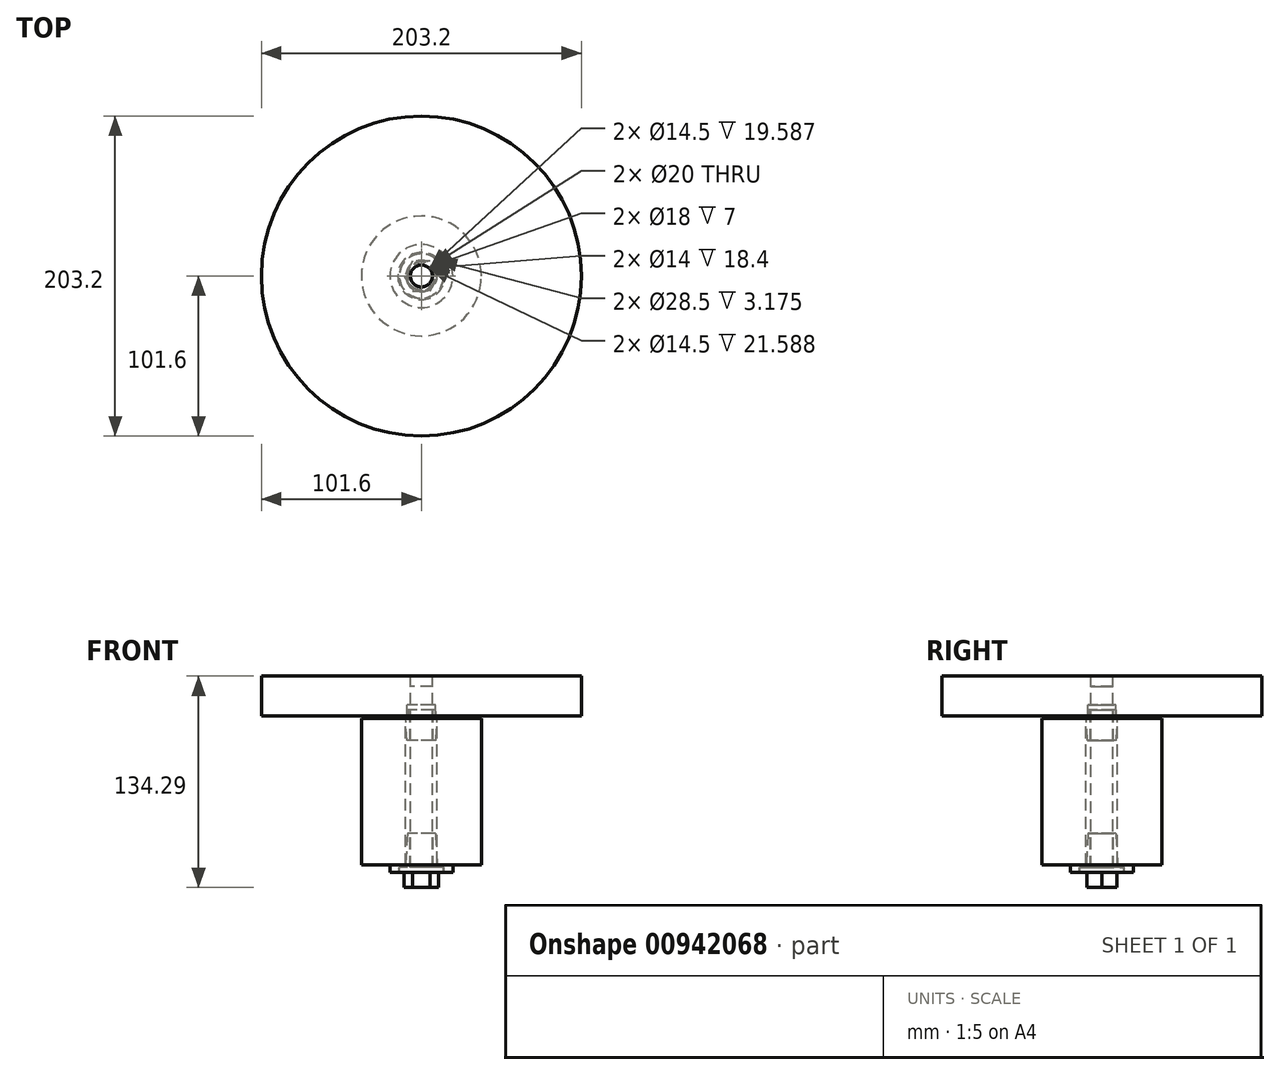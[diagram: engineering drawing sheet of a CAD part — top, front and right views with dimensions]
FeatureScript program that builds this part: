
annotation { "Feature Type Name" : "Feature", "Feature Type Description" : "" }
export const myFeature = defineFeature(function(context is Context, id is Id, definition is map)
    precondition{}
    {
        {
            var Q0;
            Q0=qCreatedBy(makeId("Front.planeOp"),FACE);
            var sketch = newSketch(context, id + "F0", { "sketchPlane" : qUnion([Q0])});
            skLineSegment(sketch, "E0", {"start": v(0, 50.8) * mm, "end": v(0, -50.8) * mm, "construction": true});
            skLineSegment(sketch, "E1.bottom", {"start": v(-101.6, 50.8) * mm, "end": v(-7, 50.8) * mm});
            skLineSegment(sketch, "E1.top", {"start": v(-101.6, 25.4) * mm, "end": v(-9, 25.4) * mm});
            skLineSegment(sketch, "E1.left", {"start": v(-101.6, 50.8) * mm, "end": v(-101.6, 25.4) * mm});
            skLineSegment(sketch, "E1.right", {"start": v(-9, 32.4) * mm, "end": v(-9, 25.4) * mm});
            skLineSegment(sketch, "E2", {"start": v(-9, 32.4) * mm, "end": v(-7, 32.4) * mm});
            skLineSegment(sketch, "E3", {"start": v(-7, 32.4) * mm, "end": v(-7, 50.8) * mm});
            skSolve(sketch);
        }
        {
            var Q0;
            Q0=makeQuery(id+"F0.imprint","IMPRINT",FACE,{"disambiguationData":[TD([[makeQuery(id+"F0.imprint","IMPRINT",EDGE,{"derivedFrom":sQuery(id+"F0.wireOp",EDGE,"E1.bottom")}),-1.0]])]});
            var Q1;
            Q1=sQuery(id+"F0.wireOp",EDGE,"E0");
            revolve(context, id + "F1", {"surfaceOperationType" : NewSurfaceOperationType.NEW, "entities" : qUnion([Q0]), "axis" : qUnion([Q1]), "revolveType" : RevolveType.FULL});
        }
        {
            var Q0;
            Q0=qCreatedBy(makeId("Front.planeOp"),FACE);
            var sketch = newSketch(context, id + "F2", { "sketchPlane" : qUnion([Q0])});
            skLineSegment(sketch, "E4.0", {"start": v(0, 50.8) * mm, "end": v(0, -50.8) * mm, "construction": true});
            skLineSegment(sketch, "E5.bottom", {"start": v(-38.1, 23.81) * mm, "end": v(-10, 23.81) * mm});
            skLineSegment(sketch, "E5.top", {"start": v(-38.1, -69.2) * mm, "end": v(-10, -69.2) * mm});
            skLineSegment(sketch, "E5.left", {"start": v(-38.1, 23.81) * mm, "end": v(-38.1, -69.2) * mm});
            skLineSegment(sketch, "E5.right", {"start": v(-10, 23.81) * mm, "end": v(-10, -69.2) * mm});
            skSolve(sketch);
        }
        {
            var Q0;
            Q0=makeQuery(id+"F2.imprint","IMPRINT",FACE,{"disambiguationData":[TD([[makeQuery(id+"F2.imprint","IMPRINT",EDGE,{"derivedFrom":sQuery(id+"F2.wireOp",EDGE,"E5.bottom")}),-1.0]])]});
            var Q1;
            Q1=sQuery(id+"F2.wireOp",EDGE,"E4.0");
            revolve(context, id + "F3", {"surfaceOperationType" : NewSurfaceOperationType.NEW, "entities" : qUnion([Q0]), "axis" : qUnion([Q1]), "revolveType" : RevolveType.FULL});
        }
        {
            var Q0;
            Q0=qCreatedBy(makeId("Front.planeOp"),FACE);
            var sketch = newSketch(context, id + "F4", { "sketchPlane" : qUnion([Q0])});
            skLineSegment(sketch, "E6.0", {"start": v(0, 50.8) * mm, "end": v(0, -50.8) * mm, "construction": true});
            skLineSegment(sketch, "E7.bottom", {"start": v(0, 44.21) * mm, "end": v(-7, 44.21) * mm});
            skLineSegment(sketch, "E7.left", {"start": v(0, 44.21) * mm, "end": v(0, -73.96) * mm});
            skLineSegment(sketch, "E7.right", {"start": v(-7, 44.21) * mm, "end": v(-7, -70.79) * mm});
            skLineSegment(sketch, "E8.bottom", {"start": v(-14, -70.79) * mm, "end": v(-7, -70.79) * mm});
            skLineSegment(sketch, "E8.top", {"start": v(-14, -73.96) * mm, "end": v(0, -73.96) * mm});
            skLineSegment(sketch, "E8.left", {"start": v(-14, -70.79) * mm, "end": v(-14, -73.96) * mm});
            skSolve(sketch);
        }
        {
            var Q0;
            Q0=makeQuery(id+"F4.imprint","IMPRINT",FACE,{"disambiguationData":[TD([[makeQuery(id+"F4.imprint","IMPRINT",EDGE,{"derivedFrom":sQuery(id+"F4.wireOp",EDGE,"E7.bottom")}),1.0]])]});
            var Q1;
            Q1=sQuery(id+"F4.wireOp",EDGE,"E7.left");
            revolve(context, id + "F5", {"surfaceOperationType" : NewSurfaceOperationType.NEW, "entities" : qUnion([Q0]), "axis" : qUnion([Q1]), "revolveType" : RevolveType.FULL});
        }
        {
            var Q0;
            Q0=makeQuery(id+"F5.opRevolve","SWEPT_FACE",FACE,{"disambiguationData":[OSD([sQuery(id+"F4.wireOp",EDGE,"E8.top")])]});
            var sketch = newSketch(context, id + "F6", { "sketchPlane" : qUnion([Q0])});
            skCircle(sketch, "E9.cCircle", {"center": v(0, 0) * mm, "radius": 9.5 * mm, "construction": true});
            skLineSegment(sketch, "E9.0", {"start": v(-5.48, 9.5) * mm, "end": v(5.48, 9.5) * mm});
            skLineSegment(sketch, "E9.1", {"start": v(5.48, 9.5) * mm, "end": v(10.97, 0) * mm});
            skLineSegment(sketch, "E9.2", {"start": v(10.97, 0) * mm, "end": v(5.48, -9.5) * mm});
            skLineSegment(sketch, "E9.3", {"start": v(5.48, -9.5) * mm, "end": v(-5.48, -9.5) * mm});
            skLineSegment(sketch, "E9.4", {"start": v(-5.48, -9.5) * mm, "end": v(-10.97, 0) * mm});
            skLineSegment(sketch, "E9.5", {"start": v(-10.97, 0) * mm, "end": v(-5.48, 9.5) * mm});
            skPoint(sketch, "E9.0.midPoint", {"position": v(0, 9.5) * mm});
            skSolve(sketch);
        }
        {
            var Q0;
            Q0=makeQuery(id+"F6.imprint","IMPRINT",FACE,{"disambiguationData":[TD([[makeQuery(id+"F6.imprint","IMPRINT",EDGE,{"derivedFrom":sQuery(id+"F6.wireOp",EDGE,"E9.0")}),-1.0]])]});
            extrude(context, id + "F7", {"entities" : qUnion([Q0]), "operationType" : NewBodyOperationType.ADD, "depth" : 9.52 * mm, "offsetDistance" : 25.4 * mm});
        }
        {
            var Q0;
            Q0=qCreatedBy(makeId("Front.planeOp"),FACE);
            var sketch = newSketch(context, id + "F8", { "sketchPlane" : qUnion([Q0])});
            skLineSegment(sketch, "E10", {"start": v(-9, 25.4) * mm, "end": v(-9, 32.4) * mm, "construction": true});
            skLineSegment(sketch, "E11", {"start": v(-10, -69.2) * mm, "end": v(-10, 23.81) * mm});
            skLineSegment(sketch, "E12", {"start": v(-7, -70.79) * mm, "end": v(-7, 44.21) * mm, "construction": true});
            skLineSegment(sketch, "E13", {"start": v(-7.25, 29.4) * mm, "end": v(-8.76, 29.4) * mm});
            skLineSegment(sketch, "E14", {"start": v(-8.76, 29.4) * mm, "end": v(-8.97, 25.4) * mm});
            skLineSegment(sketch, "E15", {"start": v(-8.97, 25.4) * mm, "end": v(-15, 25.4) * mm});
            skLineSegment(sketch, "E16", {"start": v(-15, 25.4) * mm, "end": v(-15, 23.81) * mm});
            skLineSegment(sketch, "E17", {"start": v(-15, 23.81) * mm, "end": v(-9.97, 23.81) * mm});
            skLineSegment(sketch, "E18", {"start": v(-9.97, 23.81) * mm, "end": v(-9.24, 9.81) * mm});
            skLineSegment(sketch, "E19", {"start": v(-9.24, 9.81) * mm, "end": v(-7.25, 9.81) * mm});
            skLineSegment(sketch, "E20", {"start": v(-7.25, 9.81) * mm, "end": v(-7.25, 29.4) * mm});
            skSolve(sketch);
        }
        {
            var Q0;
            Q0=makeQuery(id+"F8.imprint","IMPRINT",FACE,{"disambiguationData":[TD([[makeQuery(id+"F8.imprint","IMPRINT",EDGE,{"derivedFrom":sQuery(id+"F8.wireOp",EDGE,"E13")}),1.0]])]});
            var Q1;
            Q1=sQuery(id+"F0.wireOp",EDGE,"E0");
            revolve(context, id + "F9", {"surfaceOperationType" : NewSurfaceOperationType.NEW, "entities" : qUnion([Q0]), "axis" : qUnion([Q1]), "revolveType" : RevolveType.FULL});
        }
        {
            var Q0;
            Q0=qCreatedBy(makeId("Front.planeOp"),FACE);
            var sketch = newSketch(context, id + "F10", { "sketchPlane" : qUnion([Q0])});
            skLineSegment(sketch, "E21", {"start": v(-9.97, -69.2) * mm, "end": v(-20, -69.2) * mm});
            skLineSegment(sketch, "E22", {"start": v(-20, -69.2) * mm, "end": v(-20, -73.96) * mm});
            skLineSegment(sketch, "E23", {"start": v(-20, -73.96) * mm, "end": v(-14.25, -73.96) * mm});
            skLineSegment(sketch, "E24", {"start": v(-14.25, -73.96) * mm, "end": v(-14.25, -70.79) * mm});
            skLineSegment(sketch, "E25", {"start": v(-14.25, -70.79) * mm, "end": v(-7.25, -70.79) * mm});
            skLineSegment(sketch, "E26", {"start": v(-7.25, -49.2) * mm, "end": v(-8.93, -49.2) * mm});
            skLineSegment(sketch, "E27", {"start": v(-8.93, -49.2) * mm, "end": v(-9.97, -69.2) * mm});
            skLineSegment(sketch, "E28", {"start": v(-7.25, -49.2) * mm, "end": v(-7.25, -70.79) * mm});
            skSolve(sketch);
        }
        {
            var Q0;
            Q0=makeQuery(id+"F10.imprint","IMPRINT",FACE,{"disambiguationData":[TD([[makeQuery(id+"F10.imprint","IMPRINT",EDGE,{"derivedFrom":sQuery(id+"F10.wireOp",EDGE,"E21")}),1.0]])]});
            var Q1;
            Q1=sQuery(id+"F4.wireOp",EDGE,"E7.left");
            revolve(context, id + "F11", {"surfaceOperationType" : NewSurfaceOperationType.NEW, "entities" : qUnion([Q0]), "axis" : qUnion([Q1]), "revolveType" : RevolveType.FULL});
        }
    });
